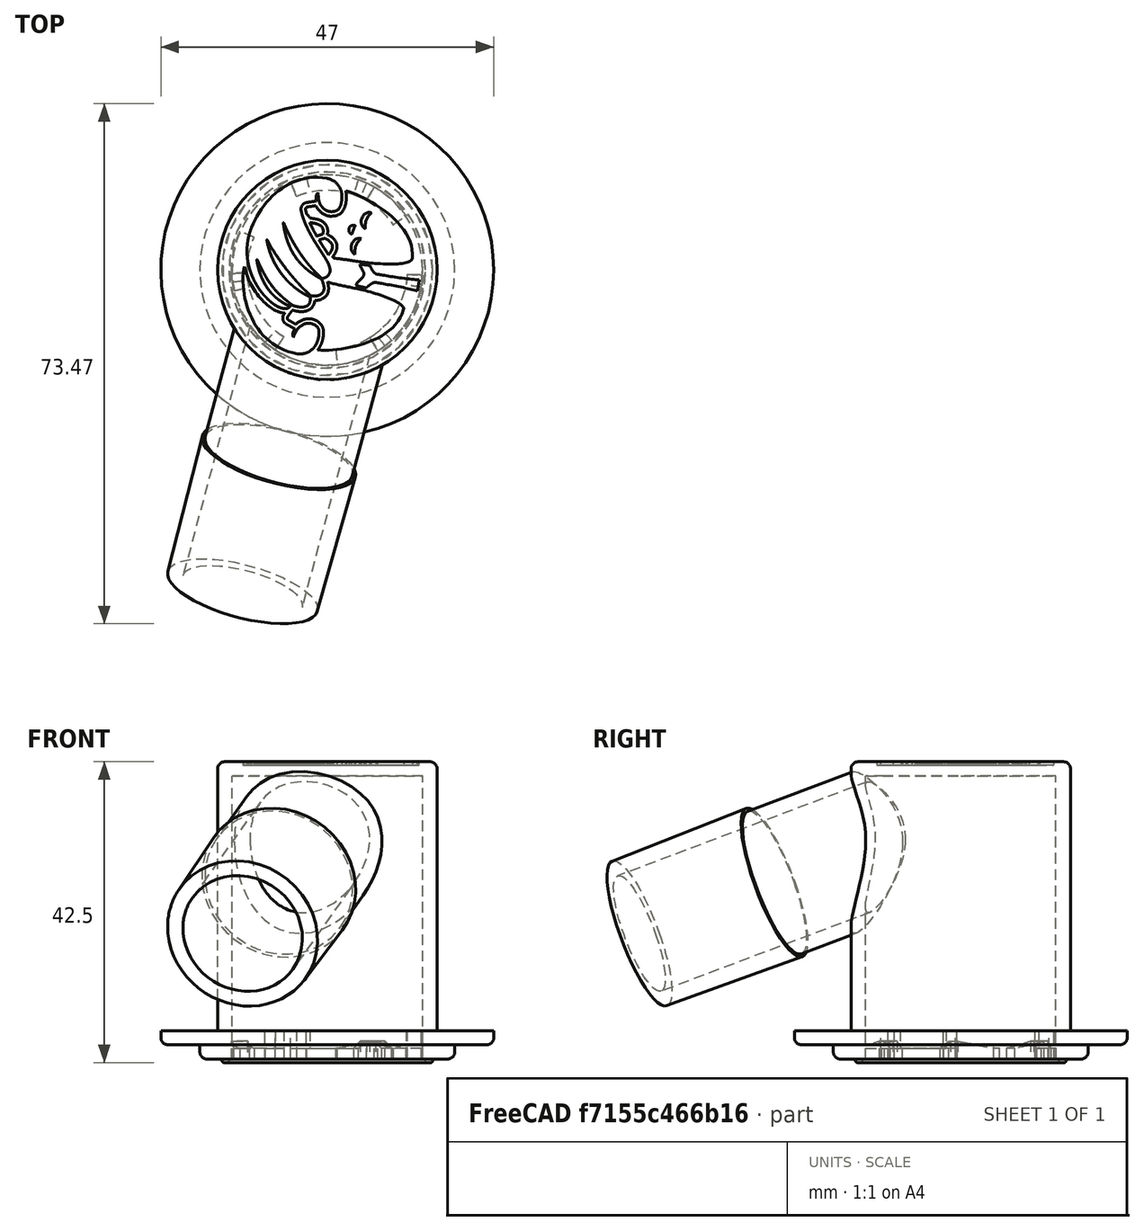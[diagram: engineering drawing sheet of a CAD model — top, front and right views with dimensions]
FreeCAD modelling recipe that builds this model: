
FCSTD DOCUMENT  (FreeCAD 0.18R4 (GitTag))
Label: PAPR-MaskAdapter-V1
License: All rights reserved
LicenseURL: http://en.wikipedia.org/wiki/All_rights_reserved
objects: Sketcher::SketchObject×40, Part::Sweep×16, Part::MultiFuse×12, Part::Feature×10, Part::Extrusion×10, Part::Cylinder×6, Part::Mirroring×5, Part::Fillet×4, Part::Cut×4, Part::FeaturePython×2, PartDesign::Body×1, Mesh::Feature×1, Part::Cone×1
note: 111 computed .brp shape members not serialized (recipe doc carries the construction recipe); baked Part::Feature solids carry a one-line shape summary decoded from their .brp

FEATURE [Sketcher::SketchObject] Sketch  label="RampStart"
  Placement = pos=(0,0,0) rot=(1,0,0;1.5708rad)
  sketch-geometry (4):
    g0: LineSegment StartX=-13.5 StartY=0 StartZ=0 EndX=-13.5 EndY=1.5 EndZ=0
    g1: LineSegment StartX=-13.5 StartY=1.5 StartZ=0 EndX=-11.3 EndY=1.5 EndZ=0
    g2: LineSegment StartX=-11.3 StartY=1.5 StartZ=0 EndX=-11.3 EndY=0 EndZ=0
    g3: LineSegment StartX=-11.3 StartY=0 StartZ=0 EndX=-13.5 EndY=0 EndZ=0
  constraints (12):
    c: Coincident(g0,g1)
    c: Coincident(g1,g2)
    c: Coincident(g2,g3)
    c: Coincident(g3,g0)
    c: Parallel(g0,g2)
    c: Parallel(g1,g3)
    c: Horizontal(g3)
    c: Vertical(g2)
    c: DistanceY(g-1,g2) = 0
    c: DistanceX(g2,g-1) = 11.3
    c: DistanceX(g0,g-1) = 13.5
    c: DistanceY(g0,g0) = 1.5
FEATURE [Sketcher::SketchObject] Sketch001  label="InnerCircumference"
  Placement = pos=(0,0,0) rot=(1,0,0;3.14159rad)
  sketch-geometry (1):
    g0: Circle CenterX=0 CenterY=0 CenterZ=0 NormalX=0 NormalY=0 NormalZ=1 AngleXU=0 Radius=11
  constraints (1):
    c: Radius(g0) = 11
FEATURE [Sketcher::SketchObject] Sketch002  label="RampEnd"
  Placement = pos=(0,0,0) rot=(0.950615,-0.219467,-0.219467;1.62142rad)
  sketch-geometry (4):
    g0: LineSegment StartX=-13.5 StartY=0 StartZ=0 EndX=-13.5 EndY=2.5 EndZ=0
    g1: LineSegment StartX=-13.5 StartY=2.5 StartZ=0 EndX=-11.3 EndY=2.5 EndZ=0
    g2: LineSegment StartX=-11.3 StartY=2.5 StartZ=0 EndX=-11.3 EndY=0 EndZ=0
    g3: LineSegment StartX=-11.3 StartY=0 StartZ=0 EndX=-13.5 EndY=0 EndZ=0
  constraints (12):
    c: Coincident(g0,g1)
    c: Coincident(g1,g2)
    c: Coincident(g2,g3)
    c: Coincident(g3,g0)
    c: Parallel(g0,g2)
    c: Parallel(g1,g3)
    c: Horizontal(g3)
    c: Vertical(g2)
    c: DistanceY(g-1,g2) = 0
    c: DistanceX(g2,g-1) = 11.3
    c: DistanceX(g0,g-1) = 13.5
    c: DistanceY(g0,g0) = 2.5
FEATURE [Sketcher::SketchObject] Sketch003  label="RampFlat"
  Placement = pos=(0,0,0) rot=(0.930118,-0.259693,-0.259693;1.64318rad)
  sketch-geometry (4):
    g0: LineSegment StartX=-13.5 StartY=0 StartZ=0 EndX=-13.5 EndY=2.5 EndZ=0
    g1: LineSegment StartX=-13.5 StartY=2.5 StartZ=0 EndX=-11.3 EndY=2.5 EndZ=0
    g2: LineSegment StartX=-11.3 StartY=2.5 StartZ=0 EndX=-11.3 EndY=0 EndZ=0
    g3: LineSegment StartX=-11.3 StartY=0 StartZ=0 EndX=-13.5 EndY=0 EndZ=0
  constraints (12):
    c: Coincident(g0,g1)
    c: Coincident(g1,g2)
    c: Coincident(g2,g3)
    c: Coincident(g3,g0)
    c: Parallel(g0,g2)
    c: Parallel(g1,g3)
    c: Horizontal(g3)
    c: Vertical(g2)
    c: DistanceY(g-1,g2) = 0
    c: DistanceX(g2,g-1) = 11.3
    c: DistanceX(g0,g-1) = 13.5
    c: DistanceY(g0,g0) = 2.5
FEATURE [Sketcher::SketchObject] Sketch004  label="LockFlat"
  Placement = pos=(0,0,0) rot=(0.906297,-0.298852,-0.298852;1.66903rad)
  sketch-geometry (4):
    g0: LineSegment StartX=-13.5 StartY=0 StartZ=0 EndX=-13.5 EndY=1.5 EndZ=0
    g1: LineSegment StartX=-13.5 StartY=1.5 StartZ=0 EndX=-11.3 EndY=1.5 EndZ=0
    g2: LineSegment StartX=-11.3 StartY=1.5 StartZ=0 EndX=-11.3 EndY=0 EndZ=0
    g3: LineSegment StartX=-11.3 StartY=0 StartZ=0 EndX=-13.5 EndY=0 EndZ=0
  constraints (12):
    c: Coincident(g0,g1)
    c: Coincident(g1,g2)
    c: Coincident(g2,g3)
    c: Coincident(g3,g0)
    c: Parallel(g0,g2)
    c: Parallel(g1,g3)
    c: Horizontal(g3)
    c: Vertical(g2)
    c: DistanceY(g-1,g2) = 0
    c: DistanceX(g2,g-1) = 11.3
    c: DistanceX(g0,g-1) = 13.5
    c: DistanceY(g0,g0) = 1.5
FEATURE [Sketcher::SketchObject] Sketch005  label="LockFlatEnd"
  Placement = pos=(0,0,0) rot=(0.638387,-0.544271,-0.544271;2.00526rad)
  sketch-geometry (4):
    g0: LineSegment StartX=-13.5 StartY=0 StartZ=0 EndX=-13.5 EndY=1.5 EndZ=0
    g1: LineSegment StartX=-13.5 StartY=1.5 StartZ=0 EndX=-11.3 EndY=1.5 EndZ=0
    g2: LineSegment StartX=-11.3 StartY=1.5 StartZ=0 EndX=-11.3 EndY=0 EndZ=0
    g3: LineSegment StartX=-11.3 StartY=0 StartZ=0 EndX=-13.5 EndY=0 EndZ=0
  constraints (12):
    c: Coincident(g0,g1)
    c: Coincident(g1,g2)
    c: Coincident(g2,g3)
    c: Coincident(g3,g0)
    c: Parallel(g0,g2)
    c: Parallel(g1,g3)
    c: Horizontal(g3)
    c: Vertical(g2)
    c: DistanceY(g-1,g2) = 0
    c: DistanceX(g2,g-1) = 11.3
    c: DistanceX(g0,g-1) = 13.5
    c: DistanceY(g0,g0) = 1.5
FEATURE [Sketcher::SketchObject] Sketch006  label="RampPath"
  sketch-geometry (1):
    g0: ArcOfCircle CenterX=0 CenterY=0 CenterZ=0 NormalX=0 NormalY=0 NormalZ=1 AngleXU=0 Radius=11.0109 StartAngle=1.68589 EndAngle=3.14182
FEATURE [Sketcher::SketchObject] Sketch007  label="Path1"
  sketch-geometry (2):
    g0: ArcOfCircle CenterX=0 CenterY=0 CenterZ=0 NormalX=0 NormalY=0 NormalZ=1 AngleXU=0 Radius=11.3 StartAngle=2.68754 EndAngle=3.14132
    g1: GeomPoint X=-10.1564 Y=4.95359 Z=0
  constraints (3):
    c: Radius(g0) = 11.3
    c: Coincident(g-1,g0)
    c: Angle(g0) = 0.453786
FEATURE [PartDesign::Body] Body
  Group = -> [Sketch005,Sketch004,Sketch003,Sketch002,Sketch001,Sketch,Sketch006,Sketch007]
  Origin = -> Origin
FEATURE [Part::Sweep] Sweep
  Frenet = false
  Sections = -> [Sketch,Sketch002]
  Solid = true
  Spine = -> Sketch007 [Edge1]
  Transition = 1
FEATURE [Sketcher::SketchObject] Sketch008  label="Path2"
  sketch-geometry (1):
    g0: ArcOfCircle CenterX=0 CenterY=0 CenterZ=0 NormalX=0 NormalY=0 NormalZ=1 AngleXU=0 Radius=11.3 StartAngle=2.59707 EndAngle=2.68754
  constraints (2):
    c: Radius(g0) = 11.3
    c: Coincident(g0,g-1)
FEATURE [Sketcher::SketchObject] Sketch009  label="Path3"
  sketch-geometry (1):
    g0: ArcOfCircle CenterX=0 CenterY=0 CenterZ=0 NormalX=0 NormalY=0 NormalZ=1 AngleXU=0 Radius=11.3 StartAngle=2.50468 EndAngle=2.59704
  constraints (2):
    c: Radius(g0) = 11.3
    c: Coincident(g0,g-1)
FEATURE [Sketcher::SketchObject] Sketch010  label="Path4"
  sketch-geometry (1):
    g0: ArcOfCircle CenterX=0 CenterY=0 CenterZ=0 NormalX=0 NormalY=0 NormalZ=1 AngleXU=0 Radius=11.3 StartAngle=1.72935 EndAngle=2.50452
  constraints (2):
    c: Radius(g0) = 11.3
    c: Coincident(g0,g-1)
FEATURE [Part::Sweep] Sweep001
  Frenet = false
  Sections = -> [Sketch002,Sketch003]
  Solid = true
  Spine = -> Sketch008 [Edge1]
  Transition = 1
FEATURE [Part::Sweep] Sweep002
  Frenet = false
  Sections = -> [Sketch003,Sketch004]
  Solid = true
  Spine = -> Sketch009 [Edge1]
  Transition = 1
FEATURE [Part::Sweep] Sweep003
  Frenet = false
  Sections = -> [Sketch004,Sketch005]
  Solid = true
  Spine = -> Sketch010 [Edge1]
  Transition = 1
FEATURE [Part::MultiFuse] Fusion  label="Ramp"
  Shapes = -> [Sweep,Sweep001,Sweep002,Sweep003]
FEATURE [Sketcher::SketchObject] Sketch011  label="EndstopEnd"
  Placement = pos=(0,0,0) rot=(0.638387,-0.544271,-0.544271;2.00526rad)
  sketch-geometry (4):
    g0: LineSegment StartX=-13.5 StartY=0 StartZ=0 EndX=-13.5 EndY=4 EndZ=0
    g1: LineSegment StartX=-13.5 StartY=4 StartZ=0 EndX=-11.3 EndY=4 EndZ=0
    g2: LineSegment StartX=-11.3 StartY=4 StartZ=0 EndX=-11.3 EndY=0 EndZ=0
    g3: LineSegment StartX=-11.3 StartY=0 StartZ=0 EndX=-13.5 EndY=0 EndZ=0
  constraints (12):
    c: Coincident(g0,g1)
    c: Coincident(g1,g2)
    c: Coincident(g2,g3)
    c: Coincident(g3,g0)
    c: Parallel(g0,g2)
    c: Parallel(g1,g3)
    c: Horizontal(g3)
    c: Vertical(g2)
    c: DistanceY(g-1,g2) = 0
    c: DistanceX(g2,g-1) = 11.3
    c: DistanceX(g0,g-1) = 13.5
    c: DistanceY(g0,g0) = 4
FEATURE [Sketcher::SketchObject] Sketch012  label="EndstopStart"
  Placement = pos=(0,0,0) rot=(0.688237,-0.512996,-0.512996;1.93602rad)
  sketch-geometry (4):
    g0: LineSegment StartX=-13.5 StartY=0 StartZ=0 EndX=-13.5 EndY=4 EndZ=0
    g1: LineSegment StartX=-13.5 StartY=4 StartZ=0 EndX=-11.3 EndY=4 EndZ=0
    g2: LineSegment StartX=-11.3 StartY=4 StartZ=0 EndX=-11.3 EndY=0 EndZ=0
    g3: LineSegment StartX=-11.3 StartY=0 StartZ=0 EndX=-13.5 EndY=0 EndZ=0
  constraints (12):
    c: Coincident(g0,g1)
    c: Coincident(g1,g2)
    c: Coincident(g2,g3)
    c: Coincident(g3,g0)
    c: Parallel(g0,g2)
    c: Parallel(g1,g3)
    c: Horizontal(g3)
    c: Vertical(g2)
    c: DistanceY(g-1,g2) = 0
    c: DistanceX(g2,g-1) = 11.3
    c: DistanceX(g0,g-1) = 13.5
    c: DistanceY(g0,g0) = 4
FEATURE [Sketcher::SketchObject] Sketch013  label="EndstopPath"
  sketch-geometry (1):
    g0: ArcOfCircle CenterX=0 CenterY=0 CenterZ=0 NormalX=0 NormalY=0 NormalZ=1 AngleXU=0 Radius=11.3 StartAngle=1.72959 EndAngle=1.86043
  constraints (2):
    c: Radius(g0) = 11.3
    c: Coincident(g-1,g0)
FEATURE [Part::Sweep] Sweep004  label="EndStop"
  Frenet = false
  Sections = -> [Sketch012,Sketch011]
  Solid = true
  Spine = -> Sketch013 [Edge1]
  Transition = 1
FEATURE [Part::MultiFuse] Fusion001  label="RampWithEndstop"
  Shapes = -> [Fusion,Sweep004]
FEATURE [Part::Cylinder] Cylinder001  label="pBase-Lower"
  Angle = 360
  AttacherType = Attacher::AttachEngine3D
  Height = 2
  Radius = 18
FEATURE [Part::Cylinder] Cylinder002  label="nBody-Chamber"
  Angle = 360
  AttacherType = Attacher::AttachEngine3D
  Height = 40
  Radius = 13.45
FEATURE [Sketcher::SketchObject] Sketch015  label="GrooveProfile"
  Placement = pos=(0,0,0) rot=(1,0,0;1.5708rad)
  sketch-geometry (4):
    g0: LineSegment StartX=-14.875 StartY=-0.5 StartZ=0 EndX=-13.875 EndY=-0.5 EndZ=0
    g1: LineSegment StartX=-13.875 StartY=-0.5 StartZ=0 EndX=-13.875 EndY=0.5 EndZ=0
    g2: LineSegment StartX=-13.875 StartY=0.5 StartZ=0 EndX=-14.875 EndY=0.5 EndZ=0
    g3: LineSegment StartX=-14.875 StartY=0.5 StartZ=0 EndX=-14.875 EndY=-0.5 EndZ=0
  constraints (12):
    c: Coincident(g0,g1)
    c: Coincident(g1,g2)
    c: Coincident(g2,g3)
    c: Coincident(g3,g0)
    c: Horizontal(g0)
    c: Horizontal(g2)
    c: Vertical(g1)
    c: Vertical(g3)
    c: DistanceX(g0,g0) = 1
    c: Equal(g0,g1)
    c: DistanceY(g1,g-1) = -0.5
    c: DistanceX(g1,g-1) = 13.875
FEATURE [Sketcher::SketchObject] Sketch016  label="GroovePath"
  sketch-geometry (1):
    g0: Circle CenterX=0 CenterY=0 CenterZ=0 NormalX=0 NormalY=0 NormalZ=1 AngleXU=0 Radius=13.875
  constraints (2):
    c: Coincident(g0,g-1)
    c: Radius(g0) = 13.875
FEATURE [Part::Sweep] Sweep005  label="pBase-Groove"
  Frenet = false
  Sections = -> [Sketch015]
  Solid = true
  Spine = -> Sketch016 [Edge1]
  Transition = 1
FEATURE [Part::Mirroring] Part__Mirroring  label="RampWithEndstopLong1"
  Base = (2.14696,3.57628e-07,2)
  Normal = (0,1,-1.19209e-07)
  Placement = pos=(0,0,0) rot=(0,0,-1;0.418879rad)
  Source = -> Fusion001
FEATURE [Sketcher::SketchObject] Sketch017  label="RampStart001"
  Placement = pos=(0,0,0) rot=(1,0,0;1.5708rad)
  sketch-geometry (4):
    g0: LineSegment StartX=-13.5 StartY=0 StartZ=0 EndX=-13.5 EndY=1.5 EndZ=0
    g1: LineSegment StartX=-13.5 StartY=1.5 StartZ=0 EndX=-11.3 EndY=1.5 EndZ=0
    g2: LineSegment StartX=-11.3 StartY=1.5 StartZ=0 EndX=-11.3 EndY=0 EndZ=0
    g3: LineSegment StartX=-11.3 StartY=0 StartZ=0 EndX=-13.5 EndY=0 EndZ=0
  constraints (12):
    c: Coincident(g0,g1)
    c: Coincident(g1,g2)
    c: Coincident(g2,g3)
    c: Coincident(g3,g0)
    c: Parallel(g0,g2)
    c: Parallel(g1,g3)
    c: Horizontal(g3)
    c: Vertical(g2)
    c: DistanceY(g-1,g2) = 0
    c: DistanceX(g2,g-1) = 11.3
    c: DistanceX(g0,g-1) = 13.5
    c: DistanceY(g0,g0) = 1.5
FEATURE [Sketcher::SketchObject] Sketch018  label="RampEnd001"
  Placement = pos=(0,0,0) rot=(0.950615,-0.219467,-0.219467;1.62142rad)
  sketch-geometry (4):
    g0: LineSegment StartX=-13.5 StartY=0 StartZ=0 EndX=-13.5 EndY=2.5 EndZ=0
    g1: LineSegment StartX=-13.5 StartY=2.5 StartZ=0 EndX=-11.3 EndY=2.5 EndZ=0
    g2: LineSegment StartX=-11.3 StartY=2.5 StartZ=0 EndX=-11.3 EndY=0 EndZ=0
    g3: LineSegment StartX=-11.3 StartY=0 StartZ=0 EndX=-13.5 EndY=0 EndZ=0
  constraints (12):
    c: Coincident(g0,g1)
    c: Coincident(g1,g2)
    c: Coincident(g2,g3)
    c: Coincident(g3,g0)
    c: Parallel(g0,g2)
    c: Parallel(g1,g3)
    c: Horizontal(g3)
    c: Vertical(g2)
    c: DistanceY(g-1,g2) = 0
    c: DistanceX(g2,g-1) = 11.3
    c: DistanceX(g0,g-1) = 13.5
    c: DistanceY(g0,g0) = 2.5
FEATURE [Sketcher::SketchObject] Sketch019  label="RampFlat001"
  Placement = pos=(0,0,0) rot=(0.930118,-0.259693,-0.259693;1.64318rad)
  sketch-geometry (4):
    g0: LineSegment StartX=-13.5 StartY=0 StartZ=0 EndX=-13.5 EndY=2.5 EndZ=0
    g1: LineSegment StartX=-13.5 StartY=2.5 StartZ=0 EndX=-11.3 EndY=2.5 EndZ=0
    g2: LineSegment StartX=-11.3 StartY=2.5 StartZ=0 EndX=-11.3 EndY=0 EndZ=0
    g3: LineSegment StartX=-11.3 StartY=0 StartZ=0 EndX=-13.5 EndY=0 EndZ=0
  constraints (12):
    c: Coincident(g0,g1)
    c: Coincident(g1,g2)
    c: Coincident(g2,g3)
    c: Coincident(g3,g0)
    c: Parallel(g0,g2)
    c: Parallel(g1,g3)
    c: Horizontal(g3)
    c: Vertical(g2)
    c: DistanceY(g-1,g2) = 0
    c: DistanceX(g2,g-1) = 11.3
    c: DistanceX(g0,g-1) = 13.5
    c: DistanceY(g0,g0) = 2.5
FEATURE [Sketcher::SketchObject] Sketch020  label="LockFlat001"
  Placement = pos=(0,0,0) rot=(0.906297,-0.298852,-0.298852;1.66903rad)
  sketch-geometry (4):
    g0: LineSegment StartX=-13.5 StartY=0 StartZ=0 EndX=-13.5 EndY=1.5 EndZ=0
    g1: LineSegment StartX=-13.5 StartY=1.5 StartZ=0 EndX=-11.3 EndY=1.5 EndZ=0
    g2: LineSegment StartX=-11.3 StartY=1.5 StartZ=0 EndX=-11.3 EndY=0 EndZ=0
    g3: LineSegment StartX=-11.3 StartY=0 StartZ=0 EndX=-13.5 EndY=0 EndZ=0
  constraints (12):
    c: Coincident(g0,g1)
    c: Coincident(g1,g2)
    c: Coincident(g2,g3)
    c: Coincident(g3,g0)
    c: Parallel(g0,g2)
    c: Parallel(g1,g3)
    c: Horizontal(g3)
    c: Vertical(g2)
    c: DistanceY(g-1,g2) = 0
    c: DistanceX(g2,g-1) = 11.3
    c: DistanceX(g0,g-1) = 13.5
    c: DistanceY(g0,g0) = 1.5
FEATURE [Sketcher::SketchObject] Sketch021  label="LockFlatEnd001"
  Placement = pos=(0,0,0) rot=(0.656406,-0.533447,-0.533447;1.97986rad)
  sketch-geometry (4):
    g0: LineSegment StartX=-13.5 StartY=0 StartZ=0 EndX=-13.5 EndY=1.5 EndZ=0
    g1: LineSegment StartX=-13.5 StartY=1.5 StartZ=0 EndX=-11.3 EndY=1.5 EndZ=0
    g2: LineSegment StartX=-11.3 StartY=1.5 StartZ=0 EndX=-11.3 EndY=0 EndZ=0
    g3: LineSegment StartX=-11.3 StartY=0 StartZ=0 EndX=-13.5 EndY=0 EndZ=0
  constraints (12):
    c: Coincident(g0,g1)
    c: Coincident(g1,g2)
    c: Coincident(g2,g3)
    c: Coincident(g3,g0)
    c: Parallel(g0,g2)
    c: Parallel(g1,g3)
    c: Horizontal(g3)
    c: Vertical(g2)
    c: DistanceY(g-1,g2) = 0
    c: DistanceX(g2,g-1) = 11.3
    c: DistanceX(g0,g-1) = 13.5
    c: DistanceY(g0,g0) = 1.5
FEATURE [Sketcher::SketchObject] Sketch022  label="Path005"
  sketch-geometry (2):
    g0: ArcOfCircle CenterX=0 CenterY=0 CenterZ=0 NormalX=0 NormalY=0 NormalZ=1 AngleXU=0 Radius=11.3 StartAngle=2.68754 EndAngle=3.14132
    g1: GeomPoint X=-10.1564 Y=4.95359 Z=0
  constraints (3):
    c: Radius(g0) = 11.3
    c: Coincident(g-1,g0)
    c: Angle(g0) = 0.453786
FEATURE [Sketcher::SketchObject] Sketch023  label="Path006"
  sketch-geometry (1):
    g0: ArcOfCircle CenterX=0 CenterY=0 CenterZ=0 NormalX=0 NormalY=0 NormalZ=1 AngleXU=0 Radius=11.3 StartAngle=2.59707 EndAngle=2.68754
  constraints (2):
    c: Radius(g0) = 11.3
    c: Coincident(g0,g-1)
FEATURE [Sketcher::SketchObject] Sketch024  label="Path007"
  sketch-geometry (1):
    g0: ArcOfCircle CenterX=0 CenterY=0 CenterZ=0 NormalX=0 NormalY=0 NormalZ=1 AngleXU=0 Radius=11.3 StartAngle=2.50468 EndAngle=2.59704
  constraints (2):
    c: Radius(g0) = 11.3
    c: Coincident(g0,g-1)
FEATURE [Sketcher::SketchObject] Sketch025  label="Path008"
  sketch-geometry (1):
    g0: ArcOfCircle CenterX=0 CenterY=0 CenterZ=0 NormalX=0 NormalY=0 NormalZ=1 AngleXU=0 Radius=11.3 StartAngle=1.77654 EndAngle=2.50452
  constraints (2):
    c: Radius(g0) = 11.3
    c: Coincident(g0,g-1)
FEATURE [Part::Sweep] Sweep006
  Frenet = false
  Sections = -> [Sketch018,Sketch019]
  Solid = true
  Spine = -> Sketch023 [Edge1]
  Transition = 1
FEATURE [Part::Sweep] Sweep007
  Frenet = false
  Sections = -> [Sketch019,Sketch020]
  Solid = true
  Spine = -> Sketch024 [Edge1]
  Transition = 1
FEATURE [Part::Sweep] Sweep008
  Frenet = false
  Sections = -> [Sketch020,Sketch021]
  Solid = true
  Spine = -> Sketch025 [Edge1]
  Transition = 1
FEATURE [Sketcher::SketchObject] Sketch026  label="EndstopEnd001"
  Placement = pos=(0,0,0) rot=(0.656406,-0.533447,-0.533447;1.97986rad)
  sketch-geometry (4):
    g0: LineSegment StartX=-13.5 StartY=0 StartZ=0 EndX=-13.5 EndY=4 EndZ=0
    g1: LineSegment StartX=-13.5 StartY=4 StartZ=0 EndX=-11.3 EndY=4 EndZ=0
    g2: LineSegment StartX=-11.3 StartY=4 StartZ=0 EndX=-11.3 EndY=0 EndZ=0
    g3: LineSegment StartX=-11.3 StartY=0 StartZ=0 EndX=-13.5 EndY=0 EndZ=0
  constraints (12):
    c: Coincident(g0,g1)
    c: Coincident(g1,g2)
    c: Coincident(g2,g3)
    c: Coincident(g3,g0)
    c: Parallel(g0,g2)
    c: Parallel(g1,g3)
    c: Horizontal(g3)
    c: Vertical(g2)
    c: DistanceY(g-1,g2) = 0
    c: DistanceX(g2,g-1) = 11.3
    c: DistanceX(g0,g-1) = 13.5
    c: DistanceY(g0,g0) = 4
FEATURE [Sketcher::SketchObject] Sketch027  label="EndstopStart001"
  Placement = pos=(0,0,0) rot=(0.722291,-0.489028,-0.489028;1.89053rad)
  sketch-geometry (4):
    g0: LineSegment StartX=-13.5 StartY=0 StartZ=0 EndX=-13.5 EndY=4 EndZ=0
    g1: LineSegment StartX=-13.5 StartY=4 StartZ=0 EndX=-11.3 EndY=4 EndZ=0
    g2: LineSegment StartX=-11.3 StartY=4 StartZ=0 EndX=-11.3 EndY=0 EndZ=0
    g3: LineSegment StartX=-11.3 StartY=0 StartZ=0 EndX=-13.5 EndY=0 EndZ=0
  constraints (12):
    c: Coincident(g0,g1)
    c: Coincident(g1,g2)
    c: Coincident(g2,g3)
    c: Coincident(g3,g0)
    c: Parallel(g0,g2)
    c: Parallel(g1,g3)
    c: Horizontal(g3)
    c: Vertical(g2)
    c: DistanceY(g-1,g2) = 0
    c: DistanceX(g2,g-1) = 11.3
    c: DistanceX(g0,g-1) = 13.5
    c: DistanceY(g0,g0) = 4
FEATURE [Sketcher::SketchObject] Sketch028  label="EndstopPath001"
  sketch-geometry (1):
    g0: ArcOfCircle CenterX=0 CenterY=0 CenterZ=0 NormalX=0 NormalY=0 NormalZ=1 AngleXU=0 Radius=11.3 StartAngle=1.77684 EndAngle=1.95126
  constraints (2):
    c: Radius(g0) = 11.3
    c: Coincident(g-1,g0)
FEATURE [Part::Sweep] Sweep009  label="EndStop001"
  Frenet = false
  Sections = -> [Sketch027,Sketch026]
  Solid = true
  Spine = -> Sketch028 [Edge1]
  Transition = 1
FEATURE [Part::Sweep] Sweep010
  Frenet = false
  Sections = -> [Sketch017,Sketch018]
  Solid = true
  Spine = -> Sketch022 [Edge1]
  Transition = 1
FEATURE [Part::MultiFuse] Fusion003  label="Ramp001"
  Shapes = -> [Sweep010,Sweep006,Sweep007,Sweep008]
FEATURE [Part::MultiFuse] Fusion002  label="RampWithEndstopShort"
  Placement = pos=(0,0,0) rot=(0,0,1;0.139626rad)
  Shapes = -> [Fusion003,Sweep009]
FEATURE [Part::Mirroring] Part__Mirroring001  label="RampWithEndstopShort 1"
  Base = (-7.97635,3.57628e-07,2)
  Normal = (0,1,-1.19209e-07)
  Placement = pos=(0,0,0) rot=(0,0,1;3.88336rad)
  Source = -> Fusion002
FEATURE [Sketcher::SketchObject] Sketch029  label="RampStart002"
  Placement = pos=(0,0,0) rot=(1,0,0;1.5708rad)
  sketch-geometry (4):
    g0: LineSegment StartX=-13.5 StartY=0 StartZ=0 EndX=-13.5 EndY=1.5 EndZ=0
    g1: LineSegment StartX=-13.5 StartY=1.5 StartZ=0 EndX=-11.3 EndY=1.5 EndZ=0
    g2: LineSegment StartX=-11.3 StartY=1.5 StartZ=0 EndX=-11.3 EndY=0 EndZ=0
    g3: LineSegment StartX=-11.3 StartY=0 StartZ=0 EndX=-13.5 EndY=0 EndZ=0
  constraints (12):
    c: Coincident(g0,g1)
    c: Coincident(g1,g2)
    c: Coincident(g2,g3)
    c: Coincident(g3,g0)
    c: Parallel(g0,g2)
    c: Parallel(g1,g3)
    c: Horizontal(g3)
    c: Vertical(g2)
    c: DistanceY(g-1,g2) = 0
    c: DistanceX(g2,g-1) = 11.3
    c: DistanceX(g0,g-1) = 13.5
    c: DistanceY(g0,g0) = 1.5
FEATURE [Sketcher::SketchObject] Sketch030  label="RampEnd002"
  Placement = pos=(0,0,0) rot=(0.950615,-0.219467,-0.219467;1.62142rad)
  sketch-geometry (4):
    g0: LineSegment StartX=-13.5 StartY=0 StartZ=0 EndX=-13.5 EndY=2.5 EndZ=0
    g1: LineSegment StartX=-13.5 StartY=2.5 StartZ=0 EndX=-11.3 EndY=2.5 EndZ=0
    g2: LineSegment StartX=-11.3 StartY=2.5 StartZ=0 EndX=-11.3 EndY=0 EndZ=0
    g3: LineSegment StartX=-11.3 StartY=0 StartZ=0 EndX=-13.5 EndY=0 EndZ=0
  constraints (12):
    c: Coincident(g0,g1)
    c: Coincident(g1,g2)
    c: Coincident(g2,g3)
    c: Coincident(g3,g0)
    c: Parallel(g0,g2)
    c: Parallel(g1,g3)
    c: Horizontal(g3)
    c: Vertical(g2)
    c: DistanceY(g-1,g2) = 0
    c: DistanceX(g2,g-1) = 11.3
    c: DistanceX(g0,g-1) = 13.5
    c: DistanceY(g0,g0) = 2.5
FEATURE [Sketcher::SketchObject] Sketch031  label="RampFlat002"
  Placement = pos=(0,0,0) rot=(0.930118,-0.259693,-0.259693;1.64318rad)
  sketch-geometry (4):
    g0: LineSegment StartX=-13.5 StartY=0 StartZ=0 EndX=-13.5 EndY=2.5 EndZ=0
    g1: LineSegment StartX=-13.5 StartY=2.5 StartZ=0 EndX=-11.3 EndY=2.5 EndZ=0
    g2: LineSegment StartX=-11.3 StartY=2.5 StartZ=0 EndX=-11.3 EndY=0 EndZ=0
    g3: LineSegment StartX=-11.3 StartY=0 StartZ=0 EndX=-13.5 EndY=0 EndZ=0
  constraints (12):
    c: Coincident(g0,g1)
    c: Coincident(g1,g2)
    c: Coincident(g2,g3)
    c: Coincident(g3,g0)
    c: Parallel(g0,g2)
    c: Parallel(g1,g3)
    c: Horizontal(g3)
    c: Vertical(g2)
    c: DistanceY(g-1,g2) = 0
    c: DistanceX(g2,g-1) = 11.3
    c: DistanceX(g0,g-1) = 13.5
    c: DistanceY(g0,g0) = 2.5
FEATURE [Sketcher::SketchObject] Sketch032  label="LockFlat002"
  Placement = pos=(0,0,0) rot=(0.906297,-0.298852,-0.298852;1.66903rad)
  sketch-geometry (4):
    g0: LineSegment StartX=-13.5 StartY=0 StartZ=0 EndX=-13.5 EndY=1.5 EndZ=0
    g1: LineSegment StartX=-13.5 StartY=1.5 StartZ=0 EndX=-11.3 EndY=1.5 EndZ=0
    g2: LineSegment StartX=-11.3 StartY=1.5 StartZ=0 EndX=-11.3 EndY=0 EndZ=0
    g3: LineSegment StartX=-11.3 StartY=0 StartZ=0 EndX=-13.5 EndY=0 EndZ=0
  constraints (12):
    c: Coincident(g0,g1)
    c: Coincident(g1,g2)
    c: Coincident(g2,g3)
    c: Coincident(g3,g0)
    c: Parallel(g0,g2)
    c: Parallel(g1,g3)
    c: Horizontal(g3)
    c: Vertical(g2)
    c: DistanceY(g-1,g2) = 0
    c: DistanceX(g2,g-1) = 11.3
    c: DistanceX(g0,g-1) = 13.5
    c: DistanceY(g0,g0) = 1.5
FEATURE [Sketcher::SketchObject] Sketch033  label="LockFlatEnd002"
  Placement = pos=(0,0,0) rot=(0.638387,-0.544271,-0.544271;2.00526rad)
  sketch-geometry (4):
    g0: LineSegment StartX=-13.5 StartY=0 StartZ=0 EndX=-13.5 EndY=1.5 EndZ=0
    g1: LineSegment StartX=-13.5 StartY=1.5 StartZ=0 EndX=-11.3 EndY=1.5 EndZ=0
    g2: LineSegment StartX=-11.3 StartY=1.5 StartZ=0 EndX=-11.3 EndY=0 EndZ=0
    g3: LineSegment StartX=-11.3 StartY=0 StartZ=0 EndX=-13.5 EndY=0 EndZ=0
  constraints (12):
    c: Coincident(g0,g1)
    c: Coincident(g1,g2)
    c: Coincident(g2,g3)
    c: Coincident(g3,g0)
    c: Parallel(g0,g2)
    c: Parallel(g1,g3)
    c: Horizontal(g3)
    c: Vertical(g2)
    c: DistanceY(g-1,g2) = 0
    c: DistanceX(g2,g-1) = 11.3
    c: DistanceX(g0,g-1) = 13.5
    c: DistanceY(g0,g0) = 1.5
FEATURE [Sketcher::SketchObject] Sketch034  label="Path009"
  sketch-geometry (2):
    g0: ArcOfCircle CenterX=0 CenterY=0 CenterZ=0 NormalX=0 NormalY=0 NormalZ=1 AngleXU=0 Radius=11.3 StartAngle=2.68754 EndAngle=3.14132
    g1: GeomPoint X=-10.1564 Y=4.95359 Z=0
  constraints (3):
    c: Radius(g0) = 11.3
    c: Coincident(g-1,g0)
    c: Angle(g0) = 0.453786
FEATURE [Part::Sweep] Sweep011
  Frenet = false
  Sections = -> [Sketch029,Sketch030]
  Solid = true
  Spine = -> Sketch034 [Edge1]
  Transition = 1
FEATURE [Sketcher::SketchObject] Sketch035  label="Path010"
  sketch-geometry (1):
    g0: ArcOfCircle CenterX=0 CenterY=0 CenterZ=0 NormalX=0 NormalY=0 NormalZ=1 AngleXU=0 Radius=11.3 StartAngle=2.59707 EndAngle=2.68754
  constraints (2):
    c: Radius(g0) = 11.3
    c: Coincident(g0,g-1)
FEATURE [Sketcher::SketchObject] Sketch036  label="Path011"
  sketch-geometry (1):
    g0: ArcOfCircle CenterX=0 CenterY=0 CenterZ=0 NormalX=0 NormalY=0 NormalZ=1 AngleXU=0 Radius=11.3 StartAngle=2.50468 EndAngle=2.59704
  constraints (2):
    c: Radius(g0) = 11.3
    c: Coincident(g0,g-1)
FEATURE [Sketcher::SketchObject] Sketch037  label="Path012"
  sketch-geometry (1):
    g0: ArcOfCircle CenterX=0 CenterY=0 CenterZ=0 NormalX=0 NormalY=0 NormalZ=1 AngleXU=0 Radius=11.3 StartAngle=1.72961 EndAngle=2.50452
  constraints (2):
    c: Radius(g0) = 11.3
    c: Coincident(g0,g-1)
FEATURE [Part::Sweep] Sweep012
  Frenet = false
  Sections = -> [Sketch030,Sketch031]
  Solid = true
  Spine = -> Sketch035 [Edge1]
  Transition = 1
FEATURE [Part::Sweep] Sweep013
  Frenet = false
  Sections = -> [Sketch031,Sketch032]
  Solid = true
  Spine = -> Sketch036 [Edge1]
  Transition = 1
FEATURE [Part::Sweep] Sweep014
  Frenet = false
  Sections = -> [Sketch032,Sketch033]
  Solid = true
  Spine = -> Sketch037 [Edge1]
  Transition = 1
FEATURE [Part::MultiFuse] Fusion004  label="Ramp002"
  Shapes = -> [Sweep011,Sweep012,Sweep013,Sweep014]
FEATURE [Sketcher::SketchObject] Sketch038  label="EndstopEnd002"
  Placement = pos=(0,0,0) rot=(0.638387,-0.544271,-0.544271;2.00526rad)
  sketch-geometry (4):
    g0: LineSegment StartX=-13.5 StartY=0 StartZ=0 EndX=-13.5 EndY=4 EndZ=0
    g1: LineSegment StartX=-13.5 StartY=4 StartZ=0 EndX=-11.3 EndY=4 EndZ=0
    g2: LineSegment StartX=-11.3 StartY=4 StartZ=0 EndX=-11.3 EndY=0 EndZ=0
    g3: LineSegment StartX=-11.3 StartY=0 StartZ=0 EndX=-13.5 EndY=0 EndZ=0
  constraints (12):
    c: Coincident(g0,g1)
    c: Coincident(g1,g2)
    c: Coincident(g2,g3)
    c: Coincident(g3,g0)
    c: Parallel(g0,g2)
    c: Parallel(g1,g3)
    c: Horizontal(g3)
    c: Vertical(g2)
    c: DistanceY(g-1,g2) = 0
    c: DistanceX(g2,g-1) = 11.3
    c: DistanceX(g0,g-1) = 13.5
    c: DistanceY(g0,g0) = 4
FEATURE [Sketcher::SketchObject] Sketch039  label="EndstopStart002"
  Placement = pos=(0,0,0) rot=(0.688237,-0.512996,-0.512996;1.93602rad)
  sketch-geometry (4):
    g0: LineSegment StartX=-13.5 StartY=0 StartZ=0 EndX=-13.5 EndY=4 EndZ=0
    g1: LineSegment StartX=-13.5 StartY=4 StartZ=0 EndX=-11.3 EndY=4 EndZ=0
    g2: LineSegment StartX=-11.3 StartY=4 StartZ=0 EndX=-11.3 EndY=0 EndZ=0
    g3: LineSegment StartX=-11.3 StartY=0 StartZ=0 EndX=-13.5 EndY=0 EndZ=0
  constraints (12):
    c: Coincident(g0,g1)
    c: Coincident(g1,g2)
    c: Coincident(g2,g3)
    c: Coincident(g3,g0)
    c: Parallel(g0,g2)
    c: Parallel(g1,g3)
    c: Horizontal(g3)
    c: Vertical(g2)
    c: DistanceY(g-1,g2) = 0
    c: DistanceX(g2,g-1) = 11.3
    c: DistanceX(g0,g-1) = 13.5
    c: DistanceY(g0,g0) = 4
FEATURE [Sketcher::SketchObject] Sketch040  label="EndstopPath002"
  sketch-geometry (1):
    g0: ArcOfCircle CenterX=0 CenterY=0 CenterZ=0 NormalX=0 NormalY=0 NormalZ=1 AngleXU=0 Radius=11.3 StartAngle=1.72959 EndAngle=1.86043
  constraints (2):
    c: Radius(g0) = 11.3
    c: Coincident(g-1,g0)
FEATURE [Part::Sweep] Sweep015  label="EndStop002"
  Frenet = false
  Sections = -> [Sketch039,Sketch038]
  Solid = true
  Spine = -> Sketch040 [Edge1]
  Transition = 1
FEATURE [Part::MultiFuse] Fusion005  label="RampWithEndstop001"
  Shapes = -> [Fusion004,Sweep015]
FEATURE [Part::Mirroring] Part__Mirroring002  label="RampWithEndstopLong2"
  Base = (2.14696,3.57628e-07,2)
  Normal = (0,1,-1.19209e-07)
  Placement = pos=(0,0,0) rot=(0,0,1;1.67552rad)
  Source = -> Fusion005
FEATURE [Part::MultiFuse] Fusion006  label="Ramps"
  Shapes = -> [Part__Mirroring002,Part__Mirroring001,Part__Mirroring]
FEATURE [Mesh::Feature] BayonetMtestV2
  Placement = pos=(0,0,-1.8) rot=(0,0,1;1.02102rad)
FEATURE [Part::Cylinder] Cylinder003  label="pBody-Chamber"
  Angle = 360
  AttacherType = Attacher::AttachEngine3D
  Height = 42
  Radius = 15.5
FEATURE [Part::Cylinder] Cylinder004  label="pBase-Upper"
  Angle = 360
  AttacherType = Attacher::AttachEngine3D
  Height = 2
  Placement = pos=(0,0,2) rot=(0,0,1;0rad)
  Radius = 23.5
FEATURE [Part::Fillet] Fillet  label="pBody-ChamberRounded"
  Base = -> Cylinder003
  Edges = 1 edges r=1: [Edge1]
FEATURE [Part::Fillet] Fillet001  label="pBase-UpperRounded"
  Base = -> Cylinder004
  Edges = 1 edges r=1: [Edge3]
FEATURE [Part::Fillet] Fillet002  label="pBase-LowerRounded"
  Base = -> Cylinder001
  Edges = 1 edges r=1: [Edge3]
FEATURE [Part::Fillet] Fillet003  label="pBase-GrooveRounded"
  Base = -> Sweep005
  Edges = 2 edges r=0.25: [Edge1,Edge3]
FEATURE [Part::MultiFuse] Fusion007  label="pBody"
  Shapes = -> [Fillet001,Fillet002,Fillet003,Fillet]
FEATURE [Part::Cut] Cut  label="MaskAdapterBody"
  Base = -> Fusion007
  Tool = -> Cylinder002
FEATURE [Part::Cylinder] Cylinder019  label="HousingOutlet"
  Angle = 360
  AttacherType = Attacher::AttachEngine3D
  Height = 40
  Radius = 10.75
FEATURE [Part::Cylinder] Cylinder005  label="OutletExtension"
  Angle = 360
  AttacherType = Attacher::AttachEngine3D
  Height = 40
  Radius = 8.7
FEATURE [Part::Cone] Cone001  label="22mmTaper"
  Angle = 360
  AttacherType = Attacher::AttachEngine3D
  Height = 21
  Placement = pos=(0,0,19) rot=(0,0,1;0rad)
  Radius1 = 11.19
  Radius2 = 10.92
FEATURE [Part::MultiFuse] Fusion020  label="Outside"
  Shapes = -> [Cone001,Cylinder019]
FEATURE [Part::Cut] Cut001  label="22mmHoseTaper"
  Base = -> Fusion020
  Placement = pos=(-2.23134,-9.08069,31.4174) rot=(0.107222,0.81443,-0.57027;3.29147rad)
  Tool = -> Cylinder005
FEATURE [Part::Feature] Face019
  shape: bbox 23.98 x 15.22 x 2e-07 mm, 1 faces, 0 solids (baked)
FEATURE [Part::Feature] Face021
  shape: bbox 2.22 x 2.625 x 2e-07 mm, 1 faces, 0 solids (baked)
FEATURE [Part::Feature] Face022
  shape: bbox 2.744 x 2.564 x 2e-07 mm, 1 faces, 0 solids (baked)
FEATURE [Part::Feature] Face027
  shape: bbox 3.153 x 1.741 x 2e-07 mm, 1 faces, 0 solids (baked)
FEATURE [Part::Feature] Face028
  shape: bbox 12.09 x 20.21 x 2e-07 mm, 1 faces, 0 solids (baked)
FEATURE [Part::Feature] Face020
  shape: bbox 13.56 x 15.09 x 2e-07 mm, 1 faces, 0 solids (baked)
FEATURE [Part::Extrusion] Extrude027  label="n-m-LeftEye"
  Base = -> Face027
  Dir = (0,0,-1)
  DirMode = 2
  FaceMakerClass = Part::FaceMakerBullseye
  LengthFwd = 1
  LengthRev = 0
  Solid = false
  Symmetric = false
FEATURE [Part::Extrusion] Extrude019  label="p-m-LeftHand"
  Base = -> Face019
  Dir = (0,0,-1)
  DirMode = 2
  FaceMakerClass = Part::FaceMakerBullseye
  LengthFwd = 1
  LengthRev = 0
  Solid = false
  Symmetric = false
FEATURE [Part::Extrusion] Extrude021  label="p-m-LeftFinger"
  Base = -> Face021
  Dir = (0,0,-1)
  DirMode = 2
  FaceMakerClass = Part::FaceMakerBullseye
  LengthFwd = 1
  LengthRev = 0
  Solid = false
  Symmetric = false
FEATURE [Part::Extrusion] Extrude022  label="p-m-RightFinger"
  Base = -> Face022
  Dir = (0,0,-1)
  DirMode = 2
  FaceMakerClass = Part::FaceMakerBullseye
  LengthFwd = 1
  LengthRev = 0
  Solid = false
  Symmetric = false
FEATURE [Part::Extrusion] Extrude020  label="p-m-RightHand"
  Base = -> Face020
  Dir = (0,0,-1)
  DirMode = 2
  FaceMakerClass = Part::FaceMakerBullseye
  LengthFwd = 1
  LengthRev = 0
  Solid = false
  Symmetric = false
FEATURE [Part::Extrusion] Extrude028  label="p-LeftLung"
  Base = -> Face028
  Dir = (0,0,1)
  DirMode = 2
  FaceMakerClass = Part::FaceMakerBullseye
  LengthFwd = 1
  LengthRev = 0
  Solid = false
  Symmetric = false
FEATURE [Part::Feature] Face025
  shape: bbox 3.134 x 1.688 x 2e-07 mm, 1 faces, 0 solids (baked)
FEATURE [Part::Extrusion] Extrude025  label="n-m-RightEye"
  Base = -> Face025
  Dir = (0,0,-1)
  DirMode = 2
  FaceMakerClass = Part::FaceMakerBullseye
  LengthFwd = 1
  LengthRev = 0
  Solid = false
  Symmetric = false
FEATURE [Part::Feature] Face026
  shape: bbox 1.76 x 1.081 x 2e-07 mm, 1 faces, 0 solids (baked)
FEATURE [Part::Extrusion] Extrude026  label="n-m-Mouth"
  Base = -> Face026
  Dir = (0,0,-1)
  DirMode = 2
  FaceMakerClass = Part::FaceMakerBullseye
  LengthFwd = 1
  LengthRev = 0
  Solid = false
  Symmetric = false
FEATURE [Part::MultiFuse] Fusion060  label="n-m-Face"
  Shapes = -> [Extrude027,Extrude026,Extrude025]
FEATURE [Part::Mirroring] Part__Mirroring003  label="nLogo (Mirror #1)"
  Base = (0,0,0)
  Normal = (0,0,1)
  Source = -> Fusion060
FEATURE [Part::Feature] Face023
  shape: bbox 4.011 x 10.85 x 2e-07 mm, 1 faces, 0 solids (baked)
FEATURE [Part::Extrusion] Extrude023  label="p-Trachea"
  Base = -> Face023
  Dir = (0,0,1)
  DirMode = 2
  FaceMakerClass = Part::FaceMakerBullseye
  LengthFwd = 1
  LengthRev = 0
  Solid = false
  Symmetric = false
FEATURE [Part::Feature] Face024
  shape: bbox 12.13 x 20.08 x 2e-07 mm, 1 faces, 0 solids (baked)
FEATURE [Part::Extrusion] Extrude024  label="p-m-RightLung"
  Base = -> Face024
  Dir = (0,0,-1)
  DirMode = 2
  FaceMakerClass = Part::FaceMakerBullseye
  LengthFwd = 1
  LengthRev = 0
  Solid = false
  Symmetric = false
FEATURE [Part::MultiFuse] Fusion059  label="p-m-Lungs"
  Shapes = -> [Extrude024,Extrude022,Extrude021,Extrude020,Extrude019]
FEATURE [Part::Mirroring] Part__Mirroring004  label="p-m-Lungs (Mirror #2)"
  Base = (0,0,0)
  Normal = (0,0,1)
  Source = -> Fusion059
FEATURE [Part::MultiFuse] Fusion058  label="pLogo"
  Shapes = -> [Part__Mirroring004,Extrude028,Extrude023]
FEATURE [Part::Cut] Cut019  label="Logo"
  Base = -> Fusion058
  Placement = pos=(-21,16.5,44) rot=(0,0,1;0rad)
  Tool = -> Part__Mirroring003
FEATURE [Part::FeaturePython] Clone  label="LogoCloneScaled"  # Draft clone (typed FeaturePython)
  AttacherType = Attacher::AttachEngine3D
  Fuse = false
  Objects = -> [Cut019]
  Placement = pos=(15.1672,10.911,41.5) rot=(0,0,-1;1.74533rad)
  Scale = (0.8,0.8,0.5)
FEATURE [Part::FeaturePython] Connect  label="AdapterHat"  # WARN: FeaturePython — macro-defined, semantics opaque (R4)
  Objects = -> [Cut001,Cut]
  Tolerance = 0
FEATURE [Part::Cut] Cut020  label="AdapterHatEmbossed"
  Base = -> Connect
  Tool = -> Clone
